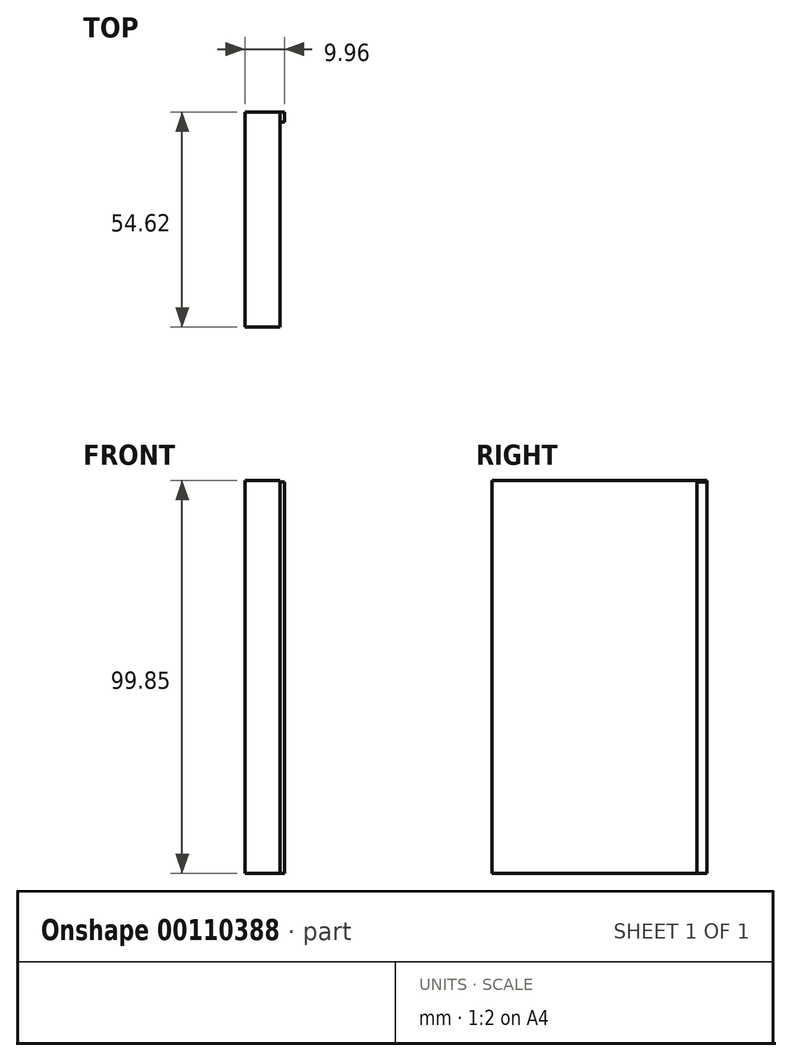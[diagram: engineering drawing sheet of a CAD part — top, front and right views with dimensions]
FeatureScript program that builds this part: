
annotation { "Feature Type Name" : "Feature", "Feature Type Description" : "" }
export const myFeature = defineFeature(function(context is Context, id is Id, definition is map)
    precondition{}
    {
        {
            var Q0;
            Q0=qCreatedBy(makeId("Front.planeOp"),FACE);
            var sketch = newSketch(context, id + "F0", { "sketchPlane" : qUnion([Q0])});
            skLineSegment(sketch, "E0.bottom", {"start": v(-39.14, 40.14) * mm, "end": v(-30.26, 40.14) * mm});
            skLineSegment(sketch, "E0.top", {"start": v(-39.14, -59.71) * mm, "end": v(-30.26, -59.71) * mm});
            skLineSegment(sketch, "E0.left", {"start": v(-39.14, 40.14) * mm, "end": v(-39.14, -59.71) * mm});
            skLineSegment(sketch, "E0.right", {"start": v(-30.26, 40.14) * mm, "end": v(-30.26, -59.71) * mm});
            skSolve(sketch);
        }
        {
            var Q0;
            Q0 = qSketchRegion(id + "F0", true);
            extrude(context, id + "F1", {"entities" : qUnion([Q0]), "depth" : 54.62 * mm});
        }
        {
            var Q0;
            Q0=qCreatedBy(makeId("Front.planeOp"),FACE);
            var sketch = newSketch(context, id + "F2", { "sketchPlane" : qUnion([Q0])});
            skLineSegment(sketch, "E1.bottom", {"start": v(-30.45, 39.78) * mm, "end": v(-29.18, 39.78) * mm});
            skLineSegment(sketch, "E1.top", {"start": v(-30.45, -59.71) * mm, "end": v(-29.18, -59.71) * mm});
            skLineSegment(sketch, "E1.left", {"start": v(-30.45, 39.78) * mm, "end": v(-30.45, -59.71) * mm});
            skLineSegment(sketch, "E1.right", {"start": v(-29.18, 39.78) * mm, "end": v(-29.18, -59.71) * mm});
            skLineSegment(sketch, "E2.top", {"start": v(-16.22, -93.33) * mm, "end": v(-14.95, -93.33) * mm});
            skSolve(sketch);
        }
        {
            var Q0;
            Q0 = qSketchRegion(id + "F2", true);
            extrude(context, id + "F3", {"entities" : qUnion([Q0]), "operationType" : NewBodyOperationType.ADD, "depth" : 2.54 * mm});
        }
    });
